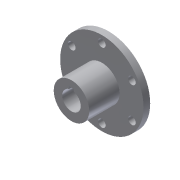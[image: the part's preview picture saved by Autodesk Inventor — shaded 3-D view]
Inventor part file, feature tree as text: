
AUTODESK INVENTOR PART (.ipt)
format: ipt  version: 2013 (Build 170138000, 138)  size: 115,200 bytes
history: native  units: in
note: dims shown in document units (in); Inventor stores cm internally (conversion verified against a paired STEP export)
features: sketch x4, extrude x3, hole x1, pattern_circular x1
ambient origin geometry x8: Origin, YZ Plane, XZ Plane, XY Plane, X Axis, Y Axis, Z Axis, Center Point
bodies: Solid1 (feature_tree)
feature tree (9):
  extrude  "Extrusion1"  Depth=0.18in TaperAngle=0.0deg
  extrude  "Extrusion2"  Depth=0.82in TaperAngle=0.0deg
  extrude  "Extrusion3"  Depth=0.125in
  hole  "Hole1"  [1 undecoded]
  pattern_circular  "Circular Pattern1"  [2 undecoded]
  sketch  "Sketch1"  dims[d0=2.25in d1=0.18in d2=0.0in]
  sketch  "Sketch2"  dims[d3=0.958in d4=0.82in d5=0.0in]
  sketch  "Sketch3"  dims[d6=0.5in d7=0.125in]
  sketch  "Sketch4"  dims[d8=0.125in d9=0.82in d10=0.0in d11=1.875in d12=0.204in d13=0.75in d14=0.375in d15=0.25in d16=0.5635in d17=1.0in d18=0.8108in d19=2.3622in d20=360.0deg]
note: 3 required parameter values undecoded (feature->parameter linkage not recoverable at this tier; creation-order binding heuristic only, values carry confidence <= 0.55)
